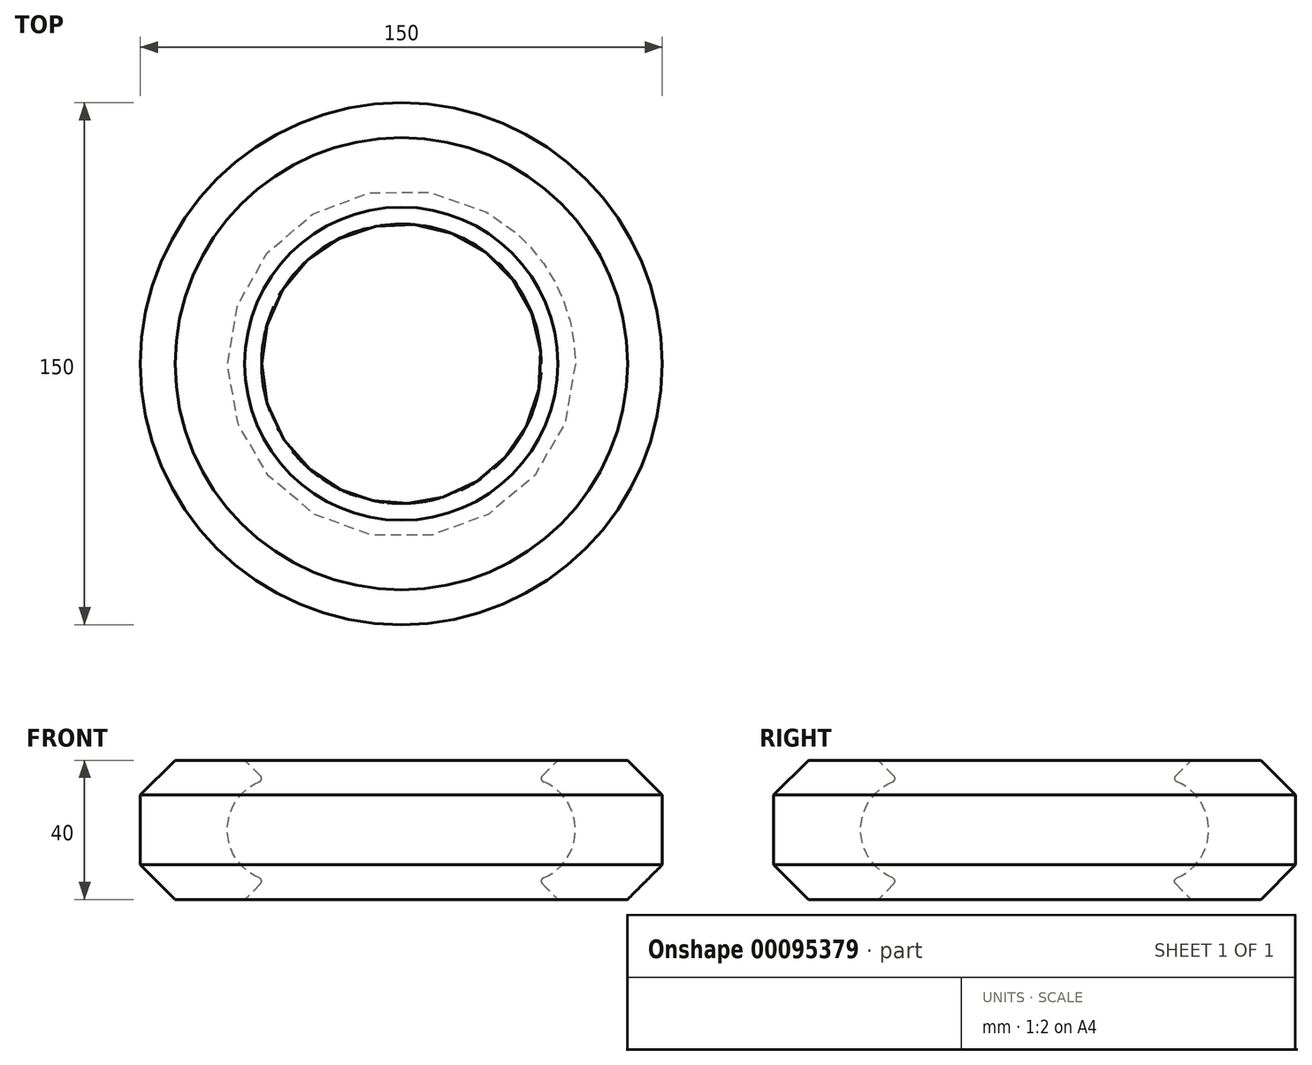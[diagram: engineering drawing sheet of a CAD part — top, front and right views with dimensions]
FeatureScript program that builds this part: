
annotation { "Feature Type Name" : "Feature", "Feature Type Description" : "" }
export const myFeature = defineFeature(function(context is Context, id is Id, definition is map)
    precondition{}
    {
        {
            var Q0;
            Q0=qCreatedBy(makeId("Front.planeOp"),FACE);
            var sketch = newSketch(context, id + "F0", { "sketchPlane" : qUnion([Q0])});
            skLineSegment(sketch, "E0", {"start": v(-35, 65.25) * mm, "end": v(-35, -20.22) * mm, "construction": true});
            skLineSegment(sketch, "E1", {"start": v(0, 0) * mm, "end": v(40, 0) * mm});
            skLineSegment(sketch, "E2", {"start": v(0, 40) * mm, "end": v(40, 40) * mm});
            skLineSegment(sketch, "E3", {"start": v(40, 40) * mm, "end": v(40, 0) * mm});
            skLineSegment(sketch, "E4", {"start": v(0, 40) * mm, "end": v(0, 35) * mm});
            skLineSegment(sketch, "E5", {"start": v(0, 0) * mm, "end": v(0, 5) * mm});
            skArc(sketch, "E6", {"start": v(0, 5) * mm, "mid": v(15, 20) * mm, "end": v(0, 35) * mm});
            skSolve(sketch);
        }
        {
            var Q0;
            Q0 = qSketchRegion(id + "F0", true);
            var Q1;
            Q1=sQuery(id+"F0.wireOp",EDGE,"E0");
            revolve(context, id + "F1", {"entities" : qUnion([Q0]), "axis" : qUnion([Q1]), "revolveType" : RevolveType.FULL});
        }
        {
            var Q0;
            Q0=makeQuery(id+"F1.opRevolve","SWEPT_EDGE",EDGE,{"disambiguationData":[OSD([sQuery(id+"F0.wireOp",EDGE,"E1"),sQuery(id+"F0.wireOp",EDGE,"E3")])]});
            var Q1;
            Q1=makeQuery(id+"F1.opRevolve","SWEPT_EDGE",EDGE,{"disambiguationData":[OSD([sQuery(id+"F0.wireOp",EDGE,"E2"),sQuery(id+"F0.wireOp",EDGE,"E3")])]});
            var Q2;
            Q2=makeQuery(id+"F1.opRevolve","SWEPT_EDGE",EDGE,{"disambiguationData":[OSD([sQuery(id+"F0.wireOp",EDGE,"UDeIGSRN-nFRX-EPOl-OaAy-qgdALyPzpkYo"),sQuery(id+"F0.wireOp",EDGE,"E1")])]});
            var Q3;
            Q3=makeQuery(id+"F1.opRevolve","SWEPT_EDGE",EDGE,{"disambiguationData":[OSD([sQuery(id+"F0.wireOp",EDGE,"gitXuNQL-AMGq-hoix-rpZY-GGmCTQceuKJc"),sQuery(id+"F0.wireOp",EDGE,"E2")])]});
            chamfer(context, id + "F2", {"entities" : qUnion([Q0, Q1, Q2, Q3]), "width" : 10 * mm, "tangentPropagation" : true});
        }
        {
            var Q0;
            Q0=makeQuery(id+"F2.opChamfer","BLEND_EDGE",EDGE,{"blendedFrom":[makeQuery(id+"F1.opRevolve","SWEPT_EDGE",EDGE,{"disambiguationData":[OSD([sQuery(id+"F0.wireOp",EDGE,"E2"),sQuery(id+"F0.wireOp",EDGE,"E4")])]}),makeQuery(id+"F1.opRevolve","SWEPT_FACE",FACE,{"disambiguationData":[OSD([sQuery(id+"F0.wireOp",EDGE,"E6")])]})],"blendedInto":[makeQuery(id+"F1.opRevolve","SWEPT_FACE",FACE,{"disambiguationData":[OSD([sQuery(id+"F0.wireOp",EDGE,"E6")])]})]});
            var Q1;
            Q1=makeQuery(id+"F2.opChamfer","BLEND_EDGE",EDGE,{"blendedFrom":[makeQuery(id+"F1.opRevolve","SWEPT_EDGE",EDGE,{"disambiguationData":[OSD([sQuery(id+"F0.wireOp",EDGE,"E1"),sQuery(id+"F0.wireOp",EDGE,"E5")])]}),makeQuery(id+"F1.opRevolve","SWEPT_FACE",FACE,{"disambiguationData":[OSD([sQuery(id+"F0.wireOp",EDGE,"E6")])]})],"blendedInto":[makeQuery(id+"F1.opRevolve","SWEPT_FACE",FACE,{"disambiguationData":[OSD([sQuery(id+"F0.wireOp",EDGE,"E6")])]})]});
            fillet(context, id + "F3", {"entities" : qUnion([Q0, Q1]), "radius" : 1 * mm, "tangentPropagation" : true, "allowEdgeOverflow" : false});
        }
    });
